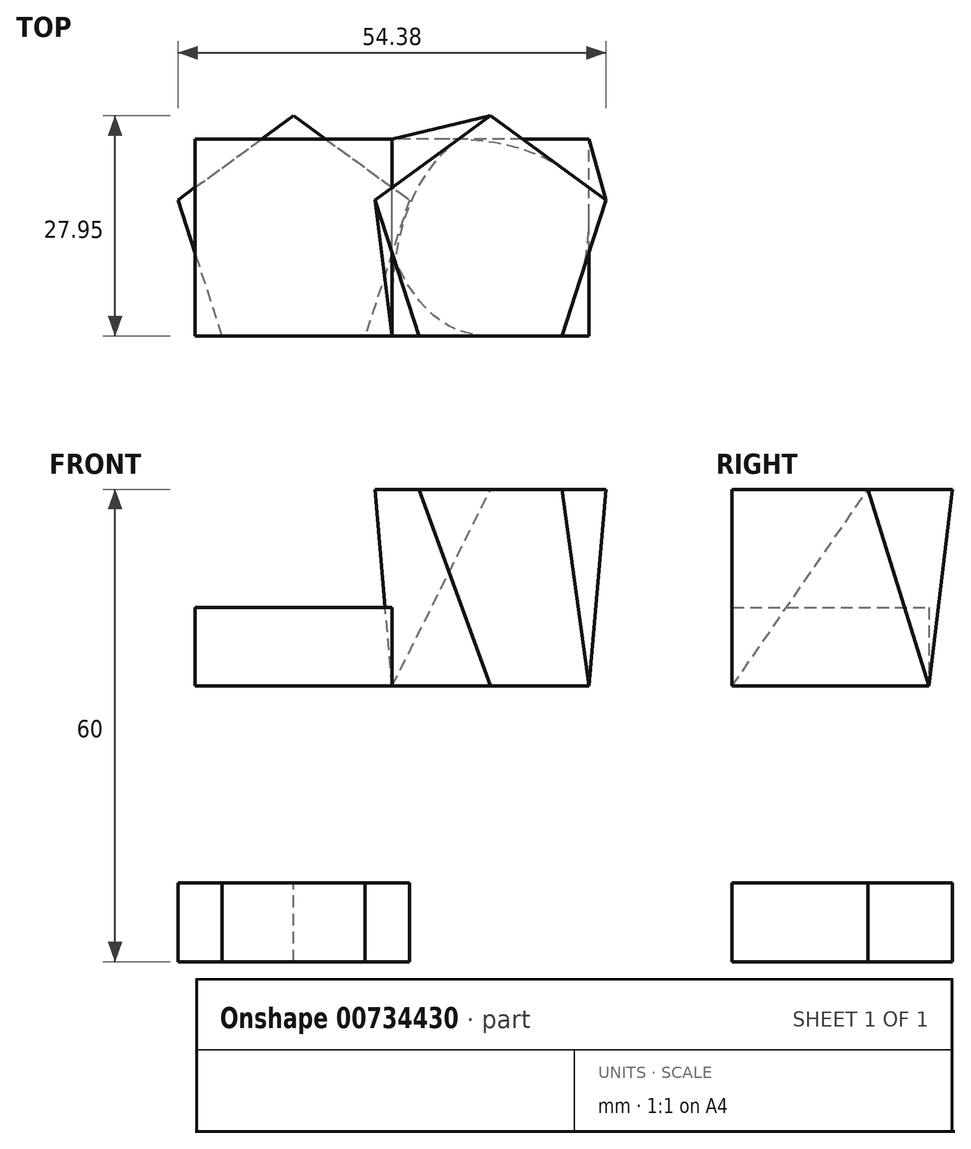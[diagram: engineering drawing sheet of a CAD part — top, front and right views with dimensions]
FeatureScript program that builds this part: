
annotation { "Feature Type Name" : "Feature", "Feature Type Description" : "" }
export const myFeature = defineFeature(function(context is Context, id is Id, definition is map)
    precondition{}
    {
        {
            var Q0;
            Q0=qCreatedBy(makeId("Top.planeOp"),FACE);
            cPlane(context, id + "F0", {"entities" : qUnion([Q0]), "cplaneType" : CPlaneType.OFFSET, "offset" : 25 * mm, "width" : 150 * mm, "height" : 150 * mm});
        }
        {
            var Q0;
            Q0=qCreatedBy(id+"F0.planeOp",FACE);
            var sketch = newSketch(context, id + "F1", { "sketchPlane" : qUnion([Q0])});
            skLineSegment(sketch, "E0.bottom", {"start": v(-12.5, -12.5) * mm, "end": v(12.5, -12.5) * mm});
            skLineSegment(sketch, "E0.top", {"start": v(-12.5, 12.5) * mm, "end": v(12.5, 12.5) * mm});
            skLineSegment(sketch, "E0.left", {"start": v(-12.5, -12.5) * mm, "end": v(-12.5, 12.5) * mm});
            skLineSegment(sketch, "E0.right", {"start": v(12.5, -12.5) * mm, "end": v(12.5, 12.5) * mm});
            skPoint(sketch, "E0.middle", {"position": v(0, 0) * mm});
            skSolve(sketch);
        }
        {
            var Q0;
            Q0=qCreatedBy(makeId("Top.planeOp"),FACE);
            var sketch = newSketch(context, id + "F2", { "sketchPlane" : qUnion([Q0])});
            skCircle(sketch, "E1.cCircle", {"center": v(0, 0) * mm, "radius": 12.5 * mm, "construction": true});
            skLineSegment(sketch, "E1.0", {"start": v(9.08, -12.5) * mm, "end": v(-9.08, -12.5) * mm});
            skLineSegment(sketch, "E1.1", {"start": v(-9.08, -12.5) * mm, "end": v(-14.7, 4.77) * mm});
            skLineSegment(sketch, "E1.2", {"start": v(-14.7, 4.77) * mm, "end": v(0, 15.45) * mm});
            skLineSegment(sketch, "E1.3", {"start": v(0, 15.45) * mm, "end": v(14.7, 4.77) * mm});
            skLineSegment(sketch, "E1.4", {"start": v(14.7, 4.77) * mm, "end": v(9.08, -12.5) * mm});
            skPoint(sketch, "E1.0.midPoint", {"position": v(0, -12.5) * mm});
            skSolve(sketch);
        }
        {
            var Q0;
            Q0=qSketchRegion(id+"F1",true);
            extrude(context, id + "F3", {"entities" : qUnion([Q0]), "depth" : 10 * mm, "offsetDistance" : 25 * mm});
        }
        {
            var Q0;
            Q0=qSketchRegion(id+"F2",true);
            extrude(context, id + "F4", {"entities" : qUnion([Q0]), "oppositeDirection" : true, "depth" : 10 * mm, "offsetDistance" : 25 * mm});
        }
        {
            var Q1;
            Q1=makeQuery(id+"F3.opExtrude","CAP_FACE",FACE,{"disambiguationData":[OSD([sQuery(id+"F1.wireOp",EDGE,"E0.bottom"),sQuery(id+"F1.wireOp",EDGE,"E0.top"),sQuery(id+"F1.wireOp",EDGE,"E0.left"),sQuery(id+"F1.wireOp",EDGE,"E0.right")])],"isStart":true});
            var Q2;
            Q2=makeQuery(id+"F4.opExtrude","CAP_FACE",FACE,{"disambiguationData":[OSD([sQuery(id+"F2.wireOp",EDGE,"E1.0"),sQuery(id+"F2.wireOp",EDGE,"E1.1"),sQuery(id+"F2.wireOp",EDGE,"E1.2"),sQuery(id+"F2.wireOp",EDGE,"E1.3"),sQuery(id+"F2.wireOp",EDGE,"E1.4")])],"isStart":true});
            var Q3;
            Q3=makeQuery(id+"F3.opExtrude","CAP_VERTEX",VERTEX,{"disambiguationData":[OSD([sQuery(id+"F1.wireOp",EDGE,"E0.top"),sQuery(id+"F1.wireOp",EDGE,"E0.left")])],"isStart":true});
            var Q4;
            Q4=makeQuery(id+"F4.opExtrude","CAP_VERTEX",VERTEX,{"disambiguationData":[OSD([sQuery(id+"F2.wireOp",EDGE,"E1.1"),sQuery(id+"F2.wireOp",EDGE,"E1.2")])],"isStart":true});
            loft(context, id + "F5", {"sheetProfilesArray" : [{ "sheetProfileEntities" : qUnion([Q1]) }, { "sheetProfileEntities" : qUnion([Q2]) }], "matchConnections" : true, "connections" : [{ "connectionEntities" : qUnion([Q3, Q4]), "connectionEdgeQueries" : qUnion([]), "connectionEdgeParameters" : [] }]});
        }
        {
            var Q0;
            Q0=makeQuery(id+"F5.opLoft","SWEPT_BODY",BODY,{"disambiguationData":[OSD([sQuery(id+"F1.wireOp",EDGE,"E0.bottom"),sQuery(id+"F1.wireOp",EDGE,"E0.top"),sQuery(id+"F1.wireOp",EDGE,"E0.left"),sQuery(id+"F1.wireOp",EDGE,"E0.right"),sQuery(id+"F2.wireOp",EDGE,"E1.0"),sQuery(id+"F2.wireOp",EDGE,"E1.1"),sQuery(id+"F2.wireOp",EDGE,"E1.2"),sQuery(id+"F2.wireOp",EDGE,"E1.3"),sQuery(id+"F2.wireOp",EDGE,"E1.4")])]});
            var Q1;
            Q1=makeQuery(id+"F5.opLoft","MID_CAP_EDGE",EDGE,{"disambiguationData":[OSD([sQuery(id+"F1.wireOp",EDGE,"E0.bottom"),sQuery(id+"F1.wireOp",EDGE,"E0.top"),sQuery(id+"F1.wireOp",EDGE,"E0.right")])],"capPos":0.0});
            transform(context, id + "F6", {"entities" : qUnion([Q0]), "transformType" : TransformType.ROTATION, "transformAxis" : qUnion([Q1]), "angle" : 180 * degree, "makeCopy" : false});
        }
    });
